# Revit family: 4L-P-ID
name_source: partatom
category: Lighting Fixtures
units: mm (PartAtom-declared; Revit-internal decimal feet)

## family parameters
Cut with Voids When Loaded = No
Host = Face
Light Source = No
OmniClass Number = 23.80.70.11.14.17
OmniClass Title = Direct/Indirect
Part Type = Normal
Room Calculation Point = No
Round Connector Dimension = Use Diameter
Shared = No

## types (6) — shared parameters
Apparent Load = 56 VA
Connector Description = Lighting Connector
Default Elevation = 48"
Description = MOD 4 LED Pendant Indirect/Direct
Direct Output/ft = D110-1100
Downlight diffuser = Downlight diffuser
Fixture Length = MOD 4 : 4'
Indirect Output/ft = I120-1200
Lamp = LED
Load Classification = Lighting
Manufacturer = Litecontrol
Model = 4L-P-ID
Pendent Height = 9"
Power Factor = 1
Product Material = Paint - Textured Camera Black
Reflector Finish = White Glass
URL = https://www.currentlighting.com
Uplight distribution = Low Peak Angle
Voltage = 120 V
Wattage Comments = Variable Intensity technology provides specifiable lumen output/wattage
Watts = 56 W

## type names (no varying parameters)
- 4L-P-ID-C1
- 4L-P-ID-C2
- 4L-P-ID-C3
- 4L-P-ID-C4
- 4L-P-ID-C5
- 4L-P-ID-C6

## geometry (parser evidence)
native form markers: Blend x6, Sweep x5
no freeform markers — native parametric forms only
